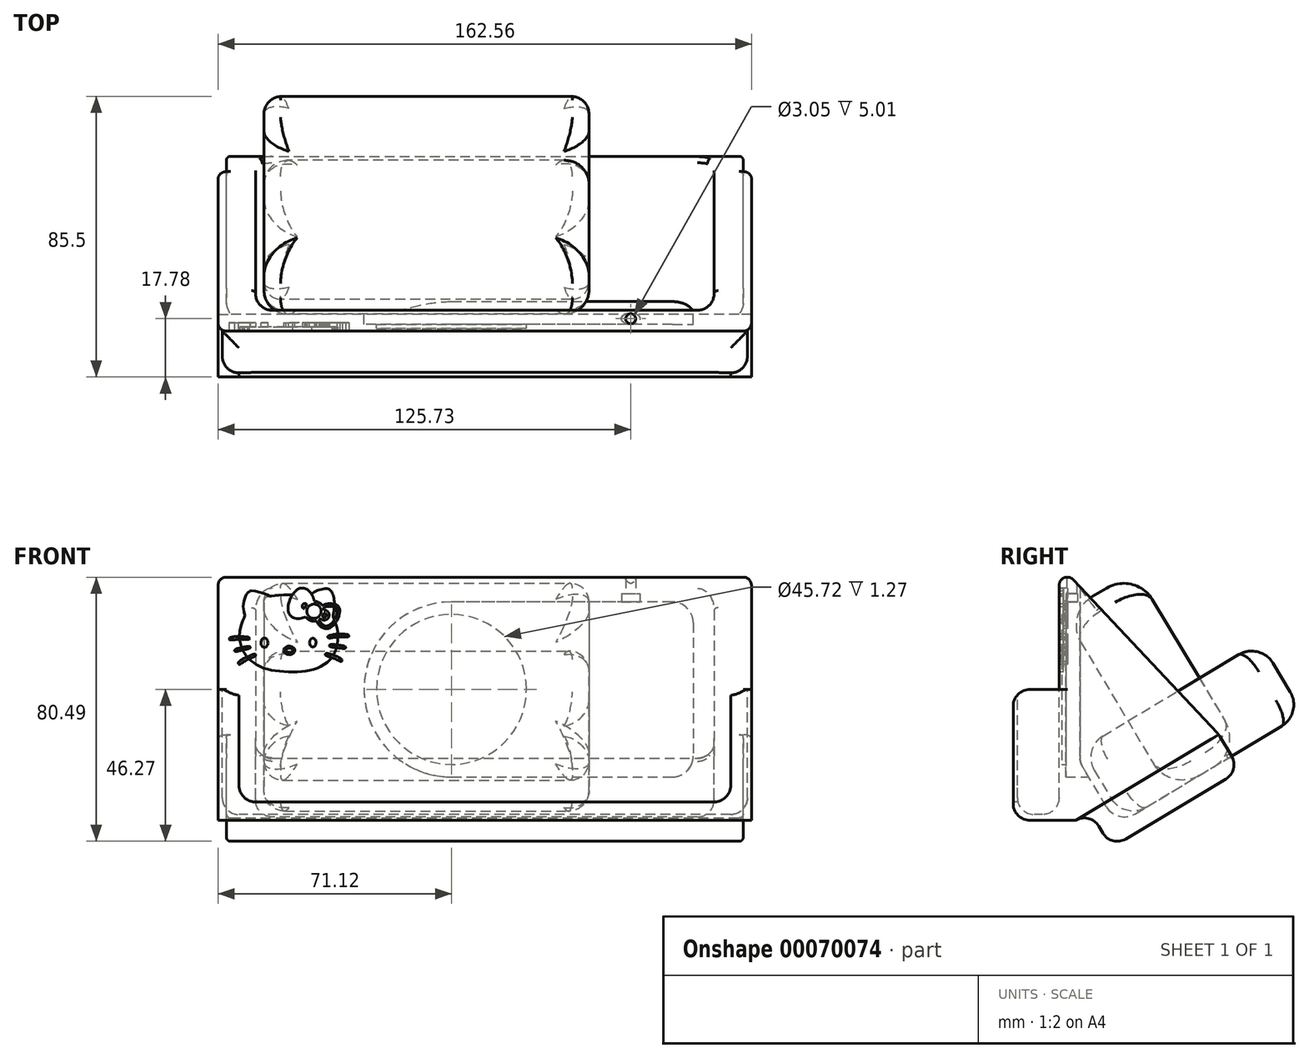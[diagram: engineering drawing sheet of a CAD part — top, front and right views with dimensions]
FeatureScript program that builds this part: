
annotation { "Feature Type Name" : "Feature", "Feature Type Description" : "" }
export const myFeature = defineFeature(function(context is Context, id is Id, definition is map)
    precondition{}
    {
        {
            var Q0;
            Q0=qCreatedBy(makeId("Right.planeOp"),FACE);
            var sketch = newSketch(context, id + "F0", { "sketchPlane" : qUnion([Q0])});
            skLineSegment(sketch, "E0", {"start": v(0, 0) * mm, "end": v(0, -76.2) * mm});
            skLineSegment(sketch, "E1", {"start": v(-13.97, -77.98) * mm, "end": v(5.08, -77.98) * mm});
            skLineSegment(sketch, "E2", {"start": v(0, -76.2) * mm, "end": v(-12.7, -76.2) * mm});
            skLineSegment(sketch, "E3", {"start": v(-12.7, -76.2) * mm, "end": v(-12.7, -72.4) * mm});
            skLineSegment(sketch, "E4", {"start": v(-12.7, -72.4) * mm, "end": v(-13.97, -72.4) * mm});
            skLineSegment(sketch, "E5", {"start": v(-13.97, -72.4) * mm, "end": v(-13.97, -77.98) * mm});
            skPoint(sketch, "E6.visualSharp", {"position": v(-12.7, -76.2) * mm});
            skPoint(sketch, "E7.visualSharp", {"position": v(0, -76.2) * mm});
            skPoint(sketch, "E8.visualSharp", {"position": v(-13.97, -77.98) * mm});
            skLineSegment(sketch, "E9", {"start": v(48.66, -51.87) * mm, "end": v(5.08, -77.98) * mm, "construction": true});
            skLineSegment(sketch, "E10", {"start": v(48.66, -51.87) * mm, "end": v(0, 0) * mm});
            skLineSegment(sketch, "E11", {"start": v(9.44, -75.37) * mm, "end": v(15.96, -86.26) * mm});
            skLineSegment(sketch, "E12", {"start": v(15.96, -86.26) * mm, "end": v(55.18, -62.76) * mm});
            skLineSegment(sketch, "E13", {"start": v(48.66, -51.87) * mm, "end": v(55.18, -62.76) * mm});
            skLineSegment(sketch, "E14", {"start": v(5.08, -77.98) * mm, "end": v(9.44, -75.37) * mm});
            skSolve(sketch);
        }
        {
            var Q0;
            Q0=qSketchRegion(id+"F0",true);
            extrude(context, id + "F1", {"entities" : qUnion([Q0]), "depth" : 81.28 * mm});
        }
        {
            var Q0;
            Q0=makeQuery(id+"F1.opExtrude","CAP_FACE",FACE,{"disambiguationData":[OSD([sQuery(id+"F0.wireOp",EDGE,"E0"),sQuery(id+"F0.wireOp",EDGE,"E1"),sQuery(id+"F0.wireOp",EDGE,"E2"),sQuery(id+"F0.wireOp",EDGE,"E3"),sQuery(id+"F0.wireOp",EDGE,"E4"),sQuery(id+"F0.wireOp",EDGE,"E5"),sQuery(id+"F0.wireOp",EDGE,"E9"),sQuery(id+"F0.wireOp",EDGE,"E10")])],"isStart":false});
            var sketch = newSketch(context, id + "F2", { "sketchPlane" : qUnion([Q0])});
            skLineSegment(sketch, "E15.bottom", {"start": v(-13.97, -77.98) * mm, "end": v(0, -77.98) * mm});
            skLineSegment(sketch, "E15.top", {"start": v(-13.97, -38.1) * mm, "end": v(0, -38.1) * mm});
            skLineSegment(sketch, "E15.left", {"start": v(-13.97, -77.98) * mm, "end": v(-13.97, -38.1) * mm});
            skLineSegment(sketch, "E15.right", {"start": v(0, -77.98) * mm, "end": v(0, -38.1) * mm});
            skSolve(sketch);
        }
        {
            var Q0;
            Q0=qSketchRegion(id+"F2",true);
            extrude(context, id + "F3", {"entities" : qUnion([Q0]), "operationType" : NewBodyOperationType.ADD, "oppositeDirection" : true, "depth" : 1.27 * mm});
        }
        {
            var Q0;
            Q0=makeQuery(id+"F3.boolean.opBoolean","MERGE",FACE,{"derivedFrom":[makeQuery(id+"F1.opExtrude","SWEPT_FACE",FACE,{"disambiguationData":[OSD([sQuery(id+"F0.wireOp",EDGE,"E5")])]}),makeQuery(id+"F3.opExtrude","SWEPT_FACE",FACE,{"disambiguationData":[OSD([sQuery(id+"F2.wireOp",EDGE,"E15.left")])]})]});
            var sketch = newSketch(context, id + "F4", { "sketchPlane" : qUnion([Q0])});
            skLineSegment(sketch, "E16.bottom", {"start": v(81.28, -77.98) * mm, "end": v(74.93, -77.98) * mm});
            skLineSegment(sketch, "E16.top", {"start": v(81.28, -38.1) * mm, "end": v(74.93, -38.1) * mm});
            skLineSegment(sketch, "E16.left", {"start": v(81.28, -77.98) * mm, "end": v(81.28, -38.1) * mm});
            skLineSegment(sketch, "E16.right", {"start": v(74.93, -77.98) * mm, "end": v(74.93, -38.1) * mm});
            skSolve(sketch);
        }
        {
            var Q0;
            Q0=qSketchRegion(id+"F4",true);
            extrude(context, id + "F5", {"entities" : qUnion([Q0]), "operationType" : NewBodyOperationType.ADD, "oppositeDirection" : true, "depth" : 1.27 * mm});
        }
        {
            var Q0;
            Q0=makeQuery(id+"F3.boolean.opBoolean","MERGE",FACE,{"derivedFrom":[makeQuery(id+"F1.opExtrude","CAP_FACE",FACE,{"disambiguationData":[OSD([sQuery(id+"F0.wireOp",EDGE,"E0"),sQuery(id+"F0.wireOp",EDGE,"E1"),sQuery(id+"F0.wireOp",EDGE,"E2"),sQuery(id+"F0.wireOp",EDGE,"E3"),sQuery(id+"F0.wireOp",EDGE,"E4"),sQuery(id+"F0.wireOp",EDGE,"E5"),sQuery(id+"F0.wireOp",EDGE,"E10"),sQuery(id+"F0.wireOp",EDGE,"E11"),sQuery(id+"F0.wireOp",EDGE,"E12"),sQuery(id+"F0.wireOp",EDGE,"E13"),sQuery(id+"F0.wireOp",EDGE,"E14")])],"isStart":false}),makeQuery(id+"F3.opExtrude","CAP_FACE",FACE,{"disambiguationData":[OSD([sQuery(id+"F2.wireOp",EDGE,"E15.bottom"),sQuery(id+"F2.wireOp",EDGE,"E15.top"),sQuery(id+"F2.wireOp",EDGE,"E15.left"),sQuery(id+"F2.wireOp",EDGE,"E15.right")])],"isStart":true})]});
            var sketch = newSketch(context, id + "F6", { "sketchPlane" : qUnion([Q0])});
            skLineSegment(sketch, "E17", {"start": v(65.06, -42.04) * mm, "end": v(-9.06, -86.45) * mm});
            skLineSegment(sketch, "E18", {"start": v(-9.06, -86.45) * mm, "end": v(1.92, -104.78) * mm});
            skLineSegment(sketch, "E19", {"start": v(1.92, -104.78) * mm, "end": v(76.04, -60.37) * mm});
            skLineSegment(sketch, "E20", {"start": v(76.04, -60.37) * mm, "end": v(65.06, -42.04) * mm});
            skSolve(sketch);
        }
        {
            var Q0;
            Q0=makeQuery(id+"F1.opExtrude","SWEPT_EDGE",EDGE,{"disambiguationData":[OSD([sQuery(id+"F0.wireOp",EDGE,"E0"),sQuery(id+"F0.wireOp",EDGE,"E10")])]});
            fillet(context, id + "F7", {"entities" : qUnion([Q0]), "radius" : 2.54 * mm, "tangentPropagation" : true, "allowEdgeOverflow" : false});
        }
        {
            var Q0;
            Q0=makeQuery(id+"F3.opExtrude","SWEPT_EDGE",EDGE,{"disambiguationData":[OSD([sQuery(id+"F0.wireOp",EDGE,"E0"),sQuery(id+"F2.wireOp",EDGE,"E15.top"),sQuery(id+"F2.wireOp",EDGE,"E15.right")])]});
            var Q1;
            Q1=makeQuery(id+"F5.boolean.opBoolean","MERGE",EDGE,{"derivedFrom":[makeQuery(id+"F3.opExtrude","SWEPT_EDGE",EDGE,{"disambiguationData":[OSD([sQuery(id+"F2.wireOp",EDGE,"E15.top"),sQuery(id+"F2.wireOp",EDGE,"E15.left")])]}),makeQuery(id+"F5.opExtrude","CAP_EDGE",EDGE,{"disambiguationData":[OSD([sQuery(id+"F4.wireOp",EDGE,"E16.top")])],"isStart":true})]});
            var Q2;
            Q2=makeQuery(id+"F5.boolean.opBoolean","INTERSECT",EDGE,{"derivedFrom":[makeQuery(id+"F1.opExtrude","SWEPT_FACE",FACE,{"disambiguationData":[OSD([sQuery(id+"F0.wireOp",EDGE,"E4")])]}),makeQuery(id+"F5.opExtrude","SWEPT_FACE",FACE,{"disambiguationData":[OSD([sQuery(id+"F4.wireOp",EDGE,"E16.right")])]})]});
            fillet(context, id + "F8", {"entities" : qUnion([Q0, Q1, Q2]), "radius" : 5.08 * mm, "tangentPropagation" : true, "allowEdgeOverflow" : false});
        }
        {
            var Q0;
            Q0=makeQuery(id+"F1.opExtrude","SWEPT_EDGE",EDGE,{"disambiguationData":[OSD([sQuery(id+"F0.wireOp",EDGE,"E0"),sQuery(id+"F0.wireOp",EDGE,"E2")])]});
            var Q1;
            Q1=makeQuery(id+"F1.opExtrude","SWEPT_EDGE",EDGE,{"disambiguationData":[OSD([sQuery(id+"F0.wireOp",EDGE,"E2"),sQuery(id+"F0.wireOp",EDGE,"E3")])]});
            var Q2;
            Q2=makeQuery(id+"F3.opExtrude","CAP_EDGE",EDGE,{"disambiguationData":[OSD([sQuery(id+"F2.wireOp",EDGE,"E15.right")])],"isStart":false});
            var Q3;
            Q3=makeQuery(id+"F5.boolean.opBoolean","INTERSECT",EDGE,{"derivedFrom":[makeQuery(id+"F3.opExtrude","CAP_FACE",FACE,{"disambiguationData":[OSD([sQuery(id+"F2.wireOp",EDGE,"E15.bottom"),sQuery(id+"F2.wireOp",EDGE,"E15.top"),sQuery(id+"F2.wireOp",EDGE,"E15.left"),sQuery(id+"F2.wireOp",EDGE,"E15.right")])],"isStart":false}),makeQuery(id+"F5.opExtrude","CAP_FACE",FACE,{"disambiguationData":[OSD([sQuery(id+"F4.wireOp",EDGE,"E16.bottom"),sQuery(id+"F4.wireOp",EDGE,"E16.top"),sQuery(id+"F4.wireOp",EDGE,"E16.left"),sQuery(id+"F4.wireOp",EDGE,"E16.right")])],"isStart":false})]});
            var Q4;
            Q4=makeQuery(id+"F3.boolean.opBoolean","INTERSECT",EDGE,{"derivedFrom":[makeQuery(id+"F1.opExtrude","SWEPT_FACE",FACE,{"disambiguationData":[OSD([sQuery(id+"F0.wireOp",EDGE,"E2")])]}),makeQuery(id+"F3.opExtrude","CAP_FACE",FACE,{"disambiguationData":[OSD([sQuery(id+"F2.wireOp",EDGE,"E15.bottom"),sQuery(id+"F2.wireOp",EDGE,"E15.top"),sQuery(id+"F2.wireOp",EDGE,"E15.left"),sQuery(id+"F2.wireOp",EDGE,"E15.right")])],"isStart":false})]});
            fillet(context, id + "F9", {"entities" : qUnion([Q0, Q1, Q2, Q3, Q4]), "radius" : 5.08 * mm, "tangentPropagation" : true, "allowEdgeOverflow" : false});
        }
        {
            var Q0;
            Q0=makeQuery(id+"FW1ILFxsN4tAGCR_1.boolean.opBoolean","COPY",EDGE,{"derivedFrom":makeQuery(id+"FW1ILFxsN4tAGCR_1.opExtrude","SWEPT_EDGE",EDGE,{"disambiguationData":[OSD([sQuery(id+"F2NUu0aQqmdHJ40_1.wireOp",EDGE,"11d1aa15-99fe-4fb5-b1c5-774e2ddcd56e.bottom"),sQuery(id+"F2NUu0aQqmdHJ40_1.wireOp",EDGE,"11d1aa15-99fe-4fb5-b1c5-774e2ddcd56e.left")])]})});
            var Q1;
            Q1=makeQuery(id+"F1.opExtrude","SWEPT_EDGE",EDGE,{"disambiguationData":[OSD([sQuery(id+"F0.wireOp",EDGE,"E1"),sQuery(id+"F0.wireOp",EDGE,"E5")])]});
            var Q2;
            Q2=makeQuery(id+"F1.opExtrude","SWEPT_EDGE",EDGE,{"disambiguationData":[OSD([sQuery(id+"F0.wireOp",EDGE,"E10"),sQuery(id+"F0.wireOp",EDGE,"E13")])]});
            var Q3;
            Q3=makeQuery(id+"F1.opExtrude","SWEPT_EDGE",EDGE,{"disambiguationData":[OSD([sQuery(id+"F0.wireOp",EDGE,"E12"),sQuery(id+"F0.wireOp",EDGE,"E13")])]});
            var Q4;
            Q4=makeQuery(id+"F1.opExtrude","SWEPT_EDGE",EDGE,{"disambiguationData":[OSD([sQuery(id+"F0.wireOp",EDGE,"E11"),sQuery(id+"F0.wireOp",EDGE,"E12")])]});
            var Q5;
            Q5=makeQuery(id+"F1.opExtrude","SWEPT_EDGE",EDGE,{"disambiguationData":[OSD([sQuery(id+"F0.wireOp",EDGE,"E11"),sQuery(id+"F0.wireOp",EDGE,"E14")])]});
            fillet(context, id + "F10", {"entities" : qUnion([Q0, Q1, Q2, Q3, Q4, Q5]), "radius" : 5.08 * mm, "tangentPropagation" : true, "allowEdgeOverflow" : false});
        }
        {
            var Q0;
            Q0=qSketchRegion(id+"F6",true);
            extrude(context, id + "F11", {"entities" : qUnion([Q0]), "operationType" : NewBodyOperationType.REMOVE, "oppositeDirection" : true, "depth" : 2.54 * mm});
        }
        {
            var Q0;
            Q0=makeQuery(id+"FW1ILFxsN4tAGCR_1.boolean.opBoolean","INTERSECT",EDGE,{"derivedFrom":[makeQuery(id+"F1.opExtrude","SWEPT_FACE",FACE,{"disambiguationData":[OSD([sQuery(id+"F0.wireOp",EDGE,"E10")])]}),makeQuery(id+"FW1ILFxsN4tAGCR_1.opExtrude","SWEPT_FACE",FACE,{"disambiguationData":[OSD([sQuery(id+"F2NUu0aQqmdHJ40_1.wireOp",EDGE,"11d1aa15-99fe-4fb5-b1c5-774e2ddcd56e.left")])]})]});
            var Q1;
            Q1=makeQuery(id+"F1.opExtrude","CAP_EDGE",EDGE,{"disambiguationData":[OSD([sQuery(id+"F0.wireOp",EDGE,"E10")])],"isStart":false});
            var Q2;
            Q2=makeQuery(id+"F11.boolean.opBoolean","COPY",EDGE,{"derivedFrom":makeQuery(id+"F11.opExtrude","CAP_EDGE",EDGE,{"disambiguationData":[OSD([sQuery(id+"F6.wireOp",EDGE,"E17")])],"isStart":true})});
            fillet(context, id + "F12", {"entities" : qUnion([Q0, Q1, Q2]), "radius" : 2.54 * mm, "tangentPropagation" : true, "allowEdgeOverflow" : false});
        }
        {
            var Q0;
            Q0=makeQuery(id+"F11.boolean.opBoolean","INTERSECT",EDGE,{"derivedFrom":[makeQuery(id+"F1.opExtrude","SWEPT_FACE",FACE,{"disambiguationData":[OSD([sQuery(id+"F0.wireOp",EDGE,"E12")])]}),makeQuery(id+"F11.opExtrude","CAP_FACE",FACE,{"disambiguationData":[OSD([sQuery(id+"F6.wireOp",EDGE,"E17"),sQuery(id+"F6.wireOp",EDGE,"E18"),sQuery(id+"F6.wireOp",EDGE,"E19"),sQuery(id+"F6.wireOp",EDGE,"E20")])],"isStart":false})]});
            fillet(context, id + "F13", {"entities" : qUnion([Q0]), "radius" : 1.27 * mm, "tangentPropagation" : true, "allowEdgeOverflow" : false});
        }
        {
            var Q0;
            Q0=makeQuery(id+"F1.opExtrude","CAP_FACE",FACE,{"disambiguationData":[OSD([sQuery(id+"F0.wireOp",EDGE,"E0"),sQuery(id+"F0.wireOp",EDGE,"E1"),sQuery(id+"F0.wireOp",EDGE,"E2"),sQuery(id+"F0.wireOp",EDGE,"E3"),sQuery(id+"F0.wireOp",EDGE,"E4"),sQuery(id+"F0.wireOp",EDGE,"E5"),sQuery(id+"F0.wireOp",EDGE,"E10"),sQuery(id+"F0.wireOp",EDGE,"E11"),sQuery(id+"F0.wireOp",EDGE,"E12"),sQuery(id+"F0.wireOp",EDGE,"E13"),sQuery(id+"F0.wireOp",EDGE,"E14")])],"isStart":true});
            var sketch = newSketch(context, id + "F14", { "sketchPlane" : qUnion([Q0])});
            skLineSegment(sketch, "E21.bottom", {"start": v(-6.35, 2.74) * mm, "end": v(-69.85, 2.74) * mm});
            skLineSegment(sketch, "E21.left", {"start": v(-6.35, 2.74) * mm, "end": v(-6.35, -58.57) * mm});
            skLineSegment(sketch, "E21.right", {"start": v(-69.85, 2.74) * mm, "end": v(-69.85, -48.06) * mm});
            skLineSegment(sketch, "E22", {"start": v(-23.16, -76.03) * mm, "end": v(-69.85, -48.06) * mm});
            skLineSegment(sketch, "E23", {"start": v(-14.45, -73.85) * mm, "end": v(-7.25, -61.84) * mm});
            skPoint(sketch, "E24.visualSharp", {"position": v(-17.71, -79.3) * mm});
            skArc(sketch, "E24.filletArc", {"start": v(-23.16, -76.03) * mm, "mid": v(-18.35, -76.74) * mm, "end": v(-14.45, -73.85) * mm});
            skPoint(sketch, "E21.top.end.orphan", {"position": v(-69.85, -98.86) * mm});
            skPoint(sketch, "E25.visualSharp", {"position": v(-6.35, -60.33) * mm});
            skArc(sketch, "E25.filletArc", {"start": v(-7.25, -61.84) * mm, "mid": v(-6.58, -60.27) * mm, "end": v(-6.35, -58.57) * mm});
            skSolve(sketch);
        }
        {
            var Q0;
            Q0 = qSketchRegion(id + "F14", true);
            extrude(context, id + "F15", {"entities" : qUnion([Q0]), "operationType" : NewBodyOperationType.REMOVE, "oppositeDirection" : true, "depth" : 69.85 * mm});
        }
        {
            var Q0;
            Q0=makeQuery(id+"F15.boolean.opBoolean","COPY",EDGE,{"derivedFrom":makeQuery(id+"F15.opExtrude","CAP_EDGE",EDGE,{"disambiguationData":[OSD([sQuery(id+"F14.wireOp",EDGE,"E22")])],"isStart":false})});
            fillet(context, id + "F16", {"entities" : qUnion([Q0]), "radius" : 5.08 * mm, "tangentPropagation" : true, "allowEdgeOverflow" : false});
        }
        {
            var Q0;
            Q0=makeQuery(id+"F15.boolean.opBoolean","INTERSECT",EDGE,{"derivedFrom":[makeQuery(id+"F1.opExtrude","SWEPT_FACE",FACE,{"disambiguationData":[OSD([sQuery(id+"F0.wireOp",EDGE,"E10")])]}),makeQuery(id+"F15.opExtrude","CAP_FACE",FACE,{"disambiguationData":[OSD([sQuery(id+"F14.wireOp",EDGE,"E21.bottom"),sQuery(id+"F14.wireOp",EDGE,"E21.left"),sQuery(id+"F14.wireOp",EDGE,"E21.right"),sQuery(id+"F14.wireOp",EDGE,"E22"),sQuery(id+"F14.wireOp",EDGE,"E23"),sQuery(id+"F14.wireOp",EDGE,"E24.filletArc"),sQuery(id+"F14.wireOp",EDGE,"E25.filletArc")])],"isStart":false})]});
            fillet(context, id + "F17", {"entities" : qUnion([Q0]), "radius" : 1.27 * mm, "tangentPropagation" : true, "allowEdgeOverflow" : false});
        }
        {
            var Q0;
            Q0=makeQuery(id+"F1.opExtrude","SWEPT_BODY",BODY,{"disambiguationData":[OSD([sQuery(id+"F0.wireOp",EDGE,"E0"),sQuery(id+"F0.wireOp",EDGE,"E1"),sQuery(id+"F0.wireOp",EDGE,"E2"),sQuery(id+"F0.wireOp",EDGE,"E3"),sQuery(id+"F0.wireOp",EDGE,"E4"),sQuery(id+"F0.wireOp",EDGE,"E5"),sQuery(id+"F0.wireOp",EDGE,"E9"),sQuery(id+"F0.wireOp",EDGE,"E10")])]});
            var Q1;
            Q1=makeQuery(id+"F1.opExtrude","CAP_FACE",FACE,{"disambiguationData":[OSD([sQuery(id+"F0.wireOp",EDGE,"E0"),sQuery(id+"F0.wireOp",EDGE,"E1"),sQuery(id+"F0.wireOp",EDGE,"E2"),sQuery(id+"F0.wireOp",EDGE,"E3"),sQuery(id+"F0.wireOp",EDGE,"E4"),sQuery(id+"F0.wireOp",EDGE,"E5"),sQuery(id+"F0.wireOp",EDGE,"E9"),sQuery(id+"F0.wireOp",EDGE,"E10")])],"isStart":true});
            mirror(context, id + "F18", {"operationType" : NewBodyOperationType.ADD, "entities" : qUnion([Q0]), "mirrorPlane" : qUnion([Q1])});
        }
        {
            var Q0;
            {var subQ0=makeQuery(id+"F1.opExtrude","SWEPT_FACE",FACE,{"disambiguationData":[OSD([sQuery(id+"F0.wireOp",EDGE,"E0")])]});Q0=makeQuery(id+"F18.boolean.opBoolean","MERGE",FACE,{"derivedFrom":[subQ0,makeQuery(id+"F18.opPattern","COPY",FACE,{"derivedFrom":subQ0,"instanceName":"1"})]});}
            var sketch = newSketch(context, id + "F19", { "sketchPlane" : qUnion([Q0])});
            skFitSpline(sketch, "E26", {"points": [v(-73.1, -15.58) * mm, v(-73.63, -13.12) * mm, v(-73.13, -10.13) * mm, v(-72.68, -9.23) * mm, v(-71.74, -8.23) * mm, v(-70.06, -8.08) * mm, v(-67.22, -8.9) * mm, v(-66.07, -9.41) * mm, v(-65.52, -9.65) * mm, v(-64.9, -9.7) * mm, v(-63.16, -9.43) * mm, v(-60.43, -9.3) * mm, v(-57.93, -9.32) * mm, v(-54.78, -9.57) * mm, v(-54.26, -9.63) * mm, v(-53.64, -9.46) * mm, v(-52.25, -8.6) * mm, v(-50.23, -7.69) * mm, v(-48.43, -7.37) * mm, v(-47.52, -7.54) * mm, v(-47.03, -7.91) * mm, v(-46.38, -9) * mm, v(-45.95, -10.69) * mm, v(-45.8, -12.09) * mm, v(-45.86, -12.9) * mm, v(-46.14, -15.06) * mm, v(-46.28, -15.8) * mm, v(-46.18, -16.16) * mm, v(-45.22, -18.72) * mm, v(-44.77, -21.3) * mm, v(-44.96, -24.23) * mm, v(-45.67, -26.7) * mm, v(-47.2, -29.08) * mm, v(-50.84, -31.5) * mm, v(-55.83, -32.64) * mm, v(-61.98, -32.61) * mm, v(-67.36, -31.58) * mm, v(-70.82, -29.62) * mm, v(-72.91, -27.53) * mm, v(-74.17, -24.96) * mm, v(-74.78, -21.77) * mm, v(-74.06, -17.98) * mm, v(-73.2, -16) * mm, v(-73.1, -15.58) * mm]});
            skFitSpline(sketch, "E27.0", {"points": [v(-72.04, -15.67) * mm, v(-72.05, -15.45) * mm, v(-72.08, -15.27) * mm, v(-72.14, -15.04) * mm, v(-72.21, -14.77) * mm, v(-72.31, -14.42) * mm, v(-72.41, -14.05) * mm, v(-72.5, -13.66) * mm, v(-72.57, -13.28) * mm, v(-72.6, -12.92) * mm, v(-72.6, -12.54) * mm, v(-72.56, -12.15) * mm, v(-72.48, -11.64) * mm, v(-72.36, -11.15) * mm, v(-72.23, -10.73) * mm, v(-72.13, -10.46) * mm, v(-72.05, -10.26) * mm, v(-71.99, -10.11) * mm, v(-71.91, -9.98) * mm, v(-71.84, -9.86) * mm, v(-71.76, -9.74) * mm, v(-71.68, -9.62) * mm, v(-71.57, -9.47) * mm, v(-71.43, -9.32) * mm, v(-71.33, -9.22) * mm, v(-71.26, -9.17) * mm, v(-71.21, -9.14) * mm, v(-71.18, -9.12) * mm, v(-71.12, -9.1) * mm, v(-71.03, -9.08) * mm, v(-70.82, -9.05) * mm, v(-70.4, -9.07) * mm, v(-69.7, -9.21) * mm, v(-68.91, -9.42) * mm, v(-68.27, -9.63) * mm, v(-67.8, -9.8) * mm, v(-67.4, -9.96) * mm, v(-66.98, -10.14) * mm, v(-66.66, -10.3) * mm, v(-66.42, -10.41) * mm, v(-66.22, -10.51) * mm, v(-65.98, -10.61) * mm, v(-65.7, -10.7) * mm, v(-65.38, -10.75) * mm, v(-65.07, -10.76) * mm, v(-64.77, -10.74) * mm, v(-64.37, -10.68) * mm, v(-63.86, -10.6) * mm, v(-63.3, -10.5) * mm, v(-62.84, -10.45) * mm, v(-62.36, -10.4) * mm, v(-61.45, -10.36) * mm, v(-60.4, -10.35) * mm, v(-59.47, -10.34) * mm, v(-58.77, -10.34) * mm, v(-57.99, -10.37) * mm, v(-57.2, -10.4) * mm, v(-56.57, -10.45) * mm, v(-56.11, -10.49) * mm, v(-55.68, -10.53) * mm, v(-55.3, -10.56) * mm, v(-55.05, -10.6) * mm, v(-54.9, -10.61) * mm, v(-54.78, -10.63) * mm, v(-54.66, -10.65) * mm, v(-54.5, -10.67) * mm, v(-54.36, -10.68) * mm, v(-54.2, -10.68) * mm, v(-54, -10.66) * mm, v(-53.74, -10.61) * mm, v(-53.48, -10.53) * mm, v(-53.28, -10.45) * mm, v(-53.07, -10.35) * mm, v(-52.83, -10.21) * mm, v(-52.55, -10.04) * mm, v(-52.28, -9.87) * mm, v(-52.02, -9.7) * mm, v(-51.75, -9.53) * mm, v(-51.4, -9.32) * mm, v(-50.91, -9.07) * mm, v(-50.32, -8.82) * mm, v(-49.72, -8.62) * mm, v(-49.14, -8.48) * mm, v(-48.7, -8.43) * mm, v(-48.43, -8.41) * mm, v(-48.26, -8.42) * mm, v(-48.12, -8.44) * mm, v(-48.01, -8.47) * mm, v(-47.94, -8.5) * mm, v(-47.91, -8.51) * mm, v(-47.9, -8.52) * mm, v(-47.85, -8.56) * mm, v(-47.76, -8.67) * mm, v(-47.66, -8.8) * mm, v(-47.55, -8.98) * mm, v(-47.45, -9.17) * mm, v(-47.36, -9.38) * mm, v(-47.24, -9.68) * mm, v(-47.12, -10.1) * mm, v(-47.03, -10.58) * mm, v(-46.96, -10.98) * mm, v(-46.92, -11.28) * mm, v(-46.88, -11.55) * mm, v(-46.86, -11.8) * mm, v(-46.85, -12.02) * mm, v(-46.84, -12.17) * mm, v(-46.85, -12.3) * mm, v(-46.87, -12.45) * mm, v(-46.9, -12.67) * mm, v(-46.94, -13.08) * mm, v(-47, -13.56) * mm, v(-47.05, -14.07) * mm, v(-47.1, -14.43) * mm, v(-47.14, -14.75) * mm, v(-47.2, -14.99) * mm, v(-47.24, -15.2) * mm, v(-47.28, -15.38) * mm, v(-47.32, -15.56) * mm, v(-47.33, -15.72) * mm, v(-47.34, -15.93) * mm, v(-47.3, -16.14) * mm, v(-47.25, -16.3) * mm, v(-47.2, -16.43) * mm, v(-47.17, -16.53) * mm, v(-47.11, -16.66) * mm, v(-47.02, -16.88) * mm, v(-46.89, -17.2) * mm, v(-46.74, -17.57) * mm, v(-46.59, -17.97) * mm, v(-46.43, -18.39) * mm, v(-46.3, -18.8) * mm, v(-46.17, -19.18) * mm, v(-46.04, -19.66) * mm, v(-45.92, -20.21) * mm, v(-45.85, -20.75) * mm, v(-45.82, -21.2) * mm, v(-45.8, -21.67) * mm, v(-45.82, -22.56) * mm, v(-45.91, -23.62) * mm, v(-46.09, -24.58) * mm, v(-46.26, -25.25) * mm, v(-46.47, -25.89) * mm, v(-46.73, -26.52) * mm, v(-47.04, -27.13) * mm, v(-47.4, -27.71) * mm, v(-47.79, -28.18) * mm, v(-48.15, -28.55) * mm, v(-48.56, -28.92) * mm, v(-49.14, -29.38) * mm, v(-49.93, -29.88) * mm, v(-50.78, -30.34) * mm, v(-51.67, -30.72) * mm, v(-52.6, -31.02) * mm, v(-53.89, -31.35) * mm, v(-55.61, -31.6) * mm, v(-57.86, -31.73) * mm, v(-59.81, -31.7) * mm, v(-61.37, -31.61) * mm, v(-62.91, -31.48) * mm, v(-64.39, -31.29) * mm, v(-65.75, -31) * mm, v(-66.7, -30.72) * mm, v(-67.56, -30.38) * mm, v(-68.65, -29.85) * mm, v(-69.62, -29.22) * mm, v(-70.5, -28.55) * mm, v(-71.08, -28.05) * mm, v(-71.59, -27.53) * mm, v(-72.02, -27) * mm, v(-72.39, -26.43) * mm, v(-72.72, -25.79) * mm, v(-73, -25.1) * mm, v(-73.27, -24.36) * mm, v(-73.49, -23.62) * mm, v(-73.65, -22.87) * mm, v(-73.72, -22.24) * mm, v(-73.73, -21.72) * mm, v(-73.72, -21.18) * mm, v(-73.64, -20.47) * mm, v(-73.46, -19.6) * mm, v(-73.27, -18.9) * mm, v(-73.09, -18.36) * mm, v(-72.94, -17.98) * mm, v(-72.8, -17.61) * mm, v(-72.65, -17.28) * mm, v(-72.5, -16.98) * mm, v(-72.38, -16.72) * mm, v(-72.3, -16.54) * mm, v(-72.24, -16.43) * mm, v(-72.18, -16.31) * mm, v(-72.11, -16.14) * mm, v(-72.06, -15.91) * mm, v(-72.04, -15.67) * mm, v(-72.05, -15.45) * mm, v(-72.08, -15.27) * mm]});
            skFitSpline(sketch, "E28", {"points": [v(-72.34, -14.3) * mm, v(-72.22, -14.48) * mm, v(-72, -14.43) * mm, v(-71.72, -14.3) * mm, v(-71.38, -14.4) * mm, v(-71.27, -14.7) * mm, v(-71.32, -15) * mm, v(-71.61, -15.41) * mm, v(-71.9, -15.87) * mm, v(-72.12, -16.15) * mm], "startDerivative": vector(0.87, -3.5) * mm, "endDerivative": vector(-1.74, -4.2) * mm});
            skSolve(sketch);
        }
        {
            var Q0;
            Q0=qSketchRegion(id+"F19",true);
            extrude(context, id + "F20", {"entities" : qUnion([Q0]), "operationType" : NewBodyOperationType.REMOVE, "oppositeDirection" : true, "depth" : 1.27 * mm});
        }
        {
            var Q0;
            Q0=makeQuery(id+"F19.imprint","IMPRINT",FACE,{"disambiguationData":[TD([[makeQuery(id+"F19.imprint","IMPRINT",EDGE,{"derivedFrom":sQuery(id+"F19.wireOp",EDGE,"E26")}),1.0]])]});
            var sketch = newSketch(context, id + "F21", { "sketchPlane" : qUnion([Q0])});
            skFitSpline(sketch, "E29", {"points": [v(-75.23, -21.92) * mm, v(-72.85, -22.06) * mm, v(-71.94, -22.25) * mm, v(-71.67, -22.52) * mm, v(-71.73, -22.73) * mm, v(-72.07, -22.88) * mm, v(-73.22, -22.82) * mm, v(-75.38, -22.84) * mm, v(-77.02, -23.01) * mm, v(-77.62, -23.01) * mm, v(-77.88, -22.9) * mm, v(-77.87, -22.54) * mm, v(-76.9, -22.1) * mm, v(-75.23, -21.92) * mm]});
            skFitSpline(sketch, "E30", {"points": [v(-74.52, -25.4) * mm, v(-72.45, -25.02) * mm, v(-71.65, -25.06) * mm, v(-71.48, -25.2) * mm, v(-71.53, -25.46) * mm, v(-71.67, -25.56) * mm, v(-72.3, -25.75) * mm, v(-74.29, -26.2) * mm, v(-75.67, -26.55) * mm, v(-76.03, -26.55) * mm, v(-76.28, -26.34) * mm, v(-76.2, -26.1) * mm, v(-75.36, -25.63) * mm, v(-74.52, -25.4) * mm]});
            skFitSpline(sketch, "E31", {"points": [v(-73.28, -28.58) * mm, v(-71.17, -27.62) * mm, v(-70.28, -27.32) * mm, v(-69.93, -27.36) * mm, v(-69.84, -27.53) * mm, v(-69.83, -27.72) * mm, v(-70.07, -27.98) * mm, v(-72.42, -29.06) * mm, v(-73.97, -30) * mm, v(-74.58, -30.41) * mm, v(-74.91, -30.4) * mm, v(-75.13, -30.25) * mm, v(-75.1, -29.9) * mm, v(-74.43, -29.25) * mm, v(-73.28, -28.58) * mm]});
            skEllipse(sketch, "E32", {"center": v(-67.16, -23.85) * mm, "majorRadius": 1.43 * mm, "minorRadius": 1.09 * mm, "majorAxis": v(0, 1)});
            skEllipse(sketch, "E33", {"center": v(-52.41, -23.8) * mm, "majorRadius": 1.34 * mm, "minorRadius": 0.98 * mm, "majorAxis": v(0, 1)});
            skEllipse(sketch, "E34", {"center": v(-59.58, -26.2) * mm, "majorRadius": 1.3 * mm, "minorRadius": 1.7 * mm, "majorAxis": v(0, 1)});
            skEllipse(sketch, "E35", {"center": v(-59.58, -26.2) * mm, "majorRadius": 0.7 * mm, "minorRadius": 1.07 * mm, "majorAxis": v(0, 1)});
            skFitSpline(sketch, "E36", {"points": [v(-47.35, -27.24) * mm, v(-45.12, -28.03) * mm, v(-43.72, -28.82) * mm, v(-43.46, -29.12) * mm, v(-43.55, -29.42) * mm, v(-43.7, -29.57) * mm, v(-44.34, -29.38) * mm, v(-46.32, -28.5) * mm, v(-48.12, -27.92) * mm, v(-48.5, -27.68) * mm, v(-48.57, -27.34) * mm, v(-48.3, -27.12) * mm, v(-47.35, -27.24) * mm]});
            skFitSpline(sketch, "E37", {"points": [v(-45.56, -24.45) * mm, v(-43.35, -24.77) * mm, v(-42.42, -25.13) * mm, v(-42.36, -25.3) * mm, v(-42.4, -25.48) * mm, v(-42.91, -25.6) * mm, v(-44.42, -25.46) * mm, v(-46.59, -25.19) * mm, v(-47.19, -24.98) * mm, v(-47.36, -24.75) * mm, v(-47.23, -24.48) * mm, v(-46.38, -24.4) * mm, v(-45.56, -24.45) * mm]});
            skFitSpline(sketch, "E38", {"points": [v(-44.68, -21.2) * mm, v(-43.6, -21.2) * mm, v(-42.23, -21.32) * mm, v(-41.52, -21.56) * mm, v(-41.4, -21.86) * mm, v(-41.64, -22.05) * mm, v(-42.64, -22.07) * mm, v(-45.04, -22.13) * mm, v(-46.24, -22.3) * mm, v(-47.4, -22.43) * mm, v(-47.77, -22.32) * mm, v(-47.87, -22.1) * mm, v(-47.8, -21.85) * mm, v(-47.34, -21.64) * mm, v(-45.56, -21.3) * mm, v(-44.68, -21.2) * mm]});
            skArc(sketch, "E39", {"start": v(-54.26, -12.19) * mm, "mid": v(-54.7, -12.8) * mm, "end": v(-54.98, -13.5) * mm});
            skCircle(sketch, "E40", {"center": v(-52.03, -14.27) * mm, "radius": 2.18 * mm});
            skArc(sketch, "E41", {"start": v(-54.26, -12.19) * mm, "mid": v(-55.57, -12.32) * mm, "end": v(-54.98, -13.5) * mm});
            skArc(sketch, "E42", {"start": v(-53.53, -11.62) * mm, "mid": v(-56.38, -11.87) * mm, "end": v(-55.07, -14.42) * mm});
            skArc(sketch, "E43", {"start": v(-49.45, -15.86) * mm, "mid": v(-48.34, -15.68) * mm, "end": v(-49.04, -14.8) * mm});
            skArc(sketch, "E44", {"start": v(-50.02, -16.54) * mm, "mid": v(-47.52, -16) * mm, "end": v(-49.01, -13.92) * mm});
            skArc(sketch, "E45.trimOffspring", {"start": v(-55.07, -14.42) * mm, "mid": v(-55.02, -14.84) * mm, "end": v(-54.91, -15.26) * mm});
            skArc(sketch, "E46.trimOffspring", {"start": v(-49.45, -15.86) * mm, "mid": v(-49.2, -15.35) * mm, "end": v(-49.04, -14.8) * mm});
            skArc(sketch, "E47.trimOffspring", {"start": v(-49.01, -13.92) * mm, "mid": v(-49.08, -13.56) * mm, "end": v(-49.18, -13.2) * mm});
            skFitSpline(sketch, "E48", {"points": [v(-51.9, -11.23) * mm, v(-52.92, -8.88) * mm, v(-55.02, -7.27) * mm, v(-56.9, -7.52) * mm, v(-58.2, -8.65) * mm, v(-59.1, -10) * mm, v(-59.89, -12.48) * mm, v(-59.87, -14.38) * mm, v(-59.1, -15.72) * mm, v(-57.8, -16.4) * mm, v(-56.06, -16.4) * mm, v(-54.56, -15.96) * mm], "startDerivative": vector(-8.54, 24.58) * mm, "endDerivative": vector(15.98, 7.04) * mm});
            skFitSpline(sketch, "E49.0", {"points": [v(-52.63, -11.49) * mm, v(-52.72, -11.22) * mm, v(-52.89, -10.73) * mm, v(-53.13, -10.08) * mm, v(-53.37, -9.6) * mm, v(-53.6, -9.26) * mm, v(-53.81, -9) * mm, v(-54.05, -8.75) * mm, v(-54.3, -8.52) * mm, v(-54.57, -8.33) * mm, v(-54.83, -8.17) * mm, v(-55.09, -8.05) * mm, v(-55.32, -7.99) * mm, v(-55.55, -7.96) * mm, v(-55.85, -7.97) * mm, v(-56.16, -8.04) * mm, v(-56.45, -8.16) * mm, v(-56.73, -8.32) * mm, v(-57.07, -8.58) * mm, v(-57.38, -8.9) * mm, v(-57.62, -9.18) * mm, v(-57.85, -9.45) * mm, v(-58.1, -9.79) * mm, v(-58.31, -10.17) * mm, v(-58.5, -10.55) * mm, v(-58.66, -10.97) * mm, v(-58.87, -11.55) * mm, v(-59.06, -12.27) * mm, v(-59.18, -12.93) * mm, v(-59.22, -13.5) * mm, v(-59.17, -14) * mm, v(-59.05, -14.44) * mm, v(-58.85, -14.84) * mm, v(-58.63, -15.1) * mm, v(-58.44, -15.28) * mm, v(-58.22, -15.42) * mm, v(-57.9, -15.57) * mm, v(-57.45, -15.68) * mm, v(-56.93, -15.71) * mm, v(-56.39, -15.68) * mm, v(-55.67, -15.55) * mm, v(-55.17, -15.37) * mm, v(-54.88, -15.24) * mm]});
            skArc(sketch, "E50.trimOffspring", {"start": v(-52.7, -11.3) * mm, "mid": v(-53.12, -11.43) * mm, "end": v(-53.53, -11.62) * mm});
            skArc(sketch, "E51.trimOffspring", {"start": v(-54.56, -15.96) * mm, "mid": v(-53.11, -17.11) * mm, "end": v(-51.26, -17.2) * mm});
            skFitSpline(sketch, "E52", {"points": [v(-49.57, -12.49) * mm, v(-47.96, -12.01) * mm, v(-45.65, -12.15) * mm, v(-44.72, -12.66) * mm, v(-44.28, -13.56) * mm, v(-44.43, -15.54) * mm, v(-45.25, -17.44) * mm, v(-46.65, -18.94) * mm, v(-48.12, -19.57) * mm, v(-49.63, -19.2) * mm, v(-50.77, -18.12) * mm, v(-51.26, -17.2) * mm], "startDerivative": vector(15.79, 6.36) * mm, "endDerivative": vector(-5.6, 12.22) * mm});
            skFitSpline(sketch, "E53.0", {"points": [v(-49.27, -13.24) * mm, v(-49.1, -13.17) * mm, v(-48.8, -13.05) * mm, v(-48.42, -12.93) * mm, v(-48.1, -12.85) * mm, v(-47.85, -12.81) * mm, v(-47.57, -12.78) * mm, v(-47.16, -12.77) * mm, v(-46.63, -12.79) * mm, v(-46.15, -12.86) * mm, v(-45.85, -12.93) * mm, v(-45.67, -12.99) * mm, v(-45.54, -13.05) * mm, v(-45.44, -13.1) * mm, v(-45.36, -13.17) * mm, v(-45.28, -13.25) * mm, v(-45.22, -13.33) * mm, v(-45.15, -13.44) * mm, v(-45.1, -13.6) * mm, v(-45.06, -13.82) * mm, v(-45.04, -14.1) * mm, v(-45.06, -14.55) * mm, v(-45.16, -15.12) * mm, v(-45.3, -15.68) * mm, v(-45.49, -16.2) * mm, v(-45.72, -16.67) * mm, v(-46.01, -17.13) * mm, v(-46.35, -17.57) * mm, v(-46.73, -17.97) * mm, v(-47.13, -18.3) * mm, v(-47.53, -18.56) * mm, v(-47.83, -18.69) * mm, v(-48.06, -18.74) * mm, v(-48.28, -18.77) * mm, v(-48.57, -18.76) * mm, v(-48.88, -18.67) * mm, v(-49.12, -18.56) * mm, v(-49.36, -18.43) * mm, v(-49.65, -18.2) * mm, v(-49.9, -17.93) * mm, v(-50.07, -17.7) * mm, v(-50.21, -17.5) * mm, v(-50.35, -17.24) * mm, v(-50.46, -17) * mm, v(-50.52, -16.87) * mm]});
            skArc(sketch, "E54.trimOffspring", {"start": v(-49.57, -12.49) * mm, "mid": v(-50.59, -11.6) * mm, "end": v(-51.9, -11.23) * mm});
            skArc(sketch, "E55.trimOffspring", {"start": v(-50.5, -16.9) * mm, "mid": v(-50.25, -16.73) * mm, "end": v(-50.02, -16.54) * mm});
            skSolve(sketch);
        }
        {
            var Q0;
            Q0=qSketchRegion(id+"F21",true);
            extrude(context, id + "F22", {"entities" : qUnion([Q0]), "operationType" : NewBodyOperationType.REMOVE, "oppositeDirection" : true, "depth" : 2.54 * mm});
        }
        {
            var Q0;
            {var subQ0=makeQuery(id+"F15.boolean.opBoolean","COPY",FACE,{"derivedFrom":makeQuery(id+"F15.opExtrude","SWEPT_FACE",FACE,{"disambiguationData":[OSD([sQuery(id+"F14.wireOp",EDGE,"E21.left")])]})});Q0=makeQuery(id+"F18.boolean.opBoolean","MERGE",FACE,{"derivedFrom":[subQ0,makeQuery(id+"F18.opPattern","COPY",FACE,{"derivedFrom":subQ0,"instanceName":"1"})]});}
            var sketch = newSketch(context, id + "F23", { "sketchPlane" : qUnion([Q0])});
            skCircle(sketch, "E56", {"center": v(10.16, -38.1) * mm, "radius": 22.86 * mm});
            skSolve(sketch);
        }
        {
            var Q0;
            Q0 = qSketchRegion(id + "F23", true);
            extrude(context, id + "F24", {"entities" : qUnion([Q0]), "operationType" : NewBodyOperationType.REMOVE, "oppositeDirection" : true, "depth" : 5.6 * mm, "hasSecondDirection" : true, "secondDirectionOppositeDirection" : false, "secondDirectionDepth" : 5.08 * mm});
        }
        {
            var Q0;
            {var subQ0=makeQuery(id+"F15.boolean.opBoolean","COPY",FACE,{"derivedFrom":makeQuery(id+"F15.opExtrude","SWEPT_FACE",FACE,{"disambiguationData":[OSD([sQuery(id+"F14.wireOp",EDGE,"E21.left")])]})});Q0=makeQuery(id+"F18.boolean.opBoolean","MERGE",FACE,{"derivedFrom":[subQ0,makeQuery(id+"F18.opPattern","COPY",FACE,{"derivedFrom":subQ0,"instanceName":"1"})]});}
            var sketch = newSketch(context, id + "F25", { "sketchPlane" : qUnion([Q0])});
            skArc(sketch, "E57", {"start": v(10.16, -64.77) * mm, "mid": v(36.83, -38.1) * mm, "end": v(10.16, -11.43) * mm});
            skLineSegment(sketch, "E58", {"start": v(-57.15, -11.43) * mm, "end": v(10.16, -11.43) * mm});
            skLineSegment(sketch, "E59", {"start": v(-63.5, -17.78) * mm, "end": v(-63.5, -58.42) * mm});
            skLineSegment(sketch, "E60", {"start": v(-57.15, -64.77) * mm, "end": v(10.16, -64.77) * mm});
            skPoint(sketch, "E61.visualSharp", {"position": v(-63.5, -11.43) * mm});
            skArc(sketch, "E61.filletArc", {"start": v(-57.15, -11.43) * mm, "mid": v(-61.64, -13.29) * mm, "end": v(-63.5, -17.78) * mm});
            skPoint(sketch, "E62.visualSharp", {"position": v(-63.5, -64.77) * mm});
            skArc(sketch, "E62.filletArc", {"start": v(-63.5, -58.42) * mm, "mid": v(-61.64, -62.91) * mm, "end": v(-57.15, -64.77) * mm});
            skSolve(sketch);
        }
        {
            var Q0;
            Q0 = qSketchRegion(id + "F25", true);
            extrude(context, id + "F26", {"entities" : qUnion([Q0]), "operationType" : NewBodyOperationType.REMOVE, "oppositeDirection" : true, "depth" : 4.32 * mm, "hasSecondDirection" : true, "secondDirectionOppositeDirection" : false, "secondDirectionDepth" : 5.08 * mm});
        }
        {
            var Q0;
            Q0=makeQuery(id+"F26.boolean.opBoolean","COPY",FACE,{"derivedFrom":makeQuery(id+"F26.opExtrude","SWEPT_FACE",FACE,{"disambiguationData":[OSD([sQuery(id+"F25.wireOp",EDGE,"E58")])]})});
            var sketch = newSketch(context, id + "F27", { "sketchPlane" : qUnion([Q0])});
            skCircle(sketch, "E63", {"center": v(44.45, -3.8) * mm, "radius": 1.52 * mm});
            skSolve(sketch);
        }
        {
            var Q0;
            Q0 = qSketchRegion(id + "F27", true);
            extrude(context, id + "F28", {"entities" : qUnion([Q0]), "operationType" : NewBodyOperationType.REMOVE, "oppositeDirection" : true, "depth" : 25.4 * mm});
        }
        {
            var Q0;
            Q0=makeQuery(id+"F26.boolean.opBoolean","COPY",FACE,{"derivedFrom":makeQuery(id+"F26.opExtrude","SWEPT_FACE",FACE,{"disambiguationData":[OSD([sQuery(id+"F25.wireOp",EDGE,"E58")])]})});
            var sketch = newSketch(context, id + "F29", { "sketchPlane" : qUnion([Q0])});
            skEllipse(sketch, "E64", {"center": v(44.45, -3.8) * mm, "majorRadius": 2.82 * mm, "minorRadius": 1.78 * mm, "majorAxis": v(-1, 0)});
            skSolve(sketch);
        }
        {
            var Q0;
            Q0 = qSketchRegion(id + "F29", true);
            extrude(context, id + "F30", {"entities" : qUnion([Q0]), "operationType" : NewBodyOperationType.REMOVE, "oppositeDirection" : true, "depth" : 2.54 * mm});
        }
        {
            var Q0;
            {var subQ0=makeQuery(id+"F15.boolean.opBoolean","COPY",FACE,{"derivedFrom":makeQuery(id+"F15.opExtrude","SWEPT_FACE",FACE,{"disambiguationData":[OSD([sQuery(id+"F14.wireOp",EDGE,"E22")])]})});Q0=makeQuery(id+"F18.boolean.opBoolean","MERGE",FACE,{"derivedFrom":[subQ0,makeQuery(id+"F18.opPattern","COPY",FACE,{"derivedFrom":subQ0,"instanceName":"1"})]});}
            var sketch = newSketch(context, id + "F31", { "sketchPlane" : qUnion([Q0])});
            skLineSegment(sketch, "E65.bottom", {"start": v(31.75, -23.02) * mm, "end": v(-67.31, -23.02) * mm});
            skLineSegment(sketch, "E65.top", {"start": v(31.75, 40.48) * mm, "end": v(-67.31, 40.48) * mm});
            skLineSegment(sketch, "E65.left", {"start": v(31.75, -23.02) * mm, "end": v(31.75, 40.48) * mm});
            skLineSegment(sketch, "E65.right", {"start": v(-67.31, -23.02) * mm, "end": v(-67.31, 40.48) * mm});
            skSolve(sketch);
        }
        {
            var Q0;
            Q0 = qSketchRegion(id + "F31", true);
            extrude(context, id + "F32", {"entities" : qUnion([Q0]), "depth" : 25.4 * mm});
        }
        {
            var Q0;
            Q0=makeQuery(id+"F32.opExtrude","SWEPT_EDGE",EDGE,{"disambiguationData":[OSD([sQuery(id+"F31.wireOp",EDGE,"E65.top"),sQuery(id+"F31.wireOp",EDGE,"E65.left")])]});
            var Q1;
            Q1=makeQuery(id+"F32.opExtrude","SWEPT_EDGE",EDGE,{"disambiguationData":[OSD([sQuery(id+"F31.wireOp",EDGE,"E65.top"),sQuery(id+"F31.wireOp",EDGE,"E65.right")])]});
            var Q2;
            Q2=makeQuery(id+"F32.opExtrude","SWEPT_EDGE",EDGE,{"disambiguationData":[OSD([sQuery(id+"F31.wireOp",EDGE,"E65.bottom"),sQuery(id+"F31.wireOp",EDGE,"E65.right")])]});
            var Q3;
            Q3=makeQuery(id+"F32.opExtrude","SWEPT_EDGE",EDGE,{"disambiguationData":[OSD([sQuery(id+"F31.wireOp",EDGE,"E65.bottom"),sQuery(id+"F31.wireOp",EDGE,"E65.left")])]});
            fillet(context, id + "F33", {"entities" : qUnion([Q0, Q1, Q2, Q3]), "radius" : 5.08 * mm, "tangentPropagation" : true, "allowEdgeOverflow" : false});
        }
        {
            var Q0;
            Q0=makeQuery(id+"F32.opExtrude","CAP_EDGE",EDGE,{"disambiguationData":[OSD([sQuery(id+"F31.wireOp",EDGE,"E65.top")])],"isStart":false});
            var Q1;
            Q1=makeQuery(id+"F32.opExtrude","CAP_EDGE",EDGE,{"disambiguationData":[OSD([sQuery(id+"F31.wireOp",EDGE,"E65.top")])],"isStart":true});
            fillet(context, id + "F34", {"entities" : qUnion([Q0, Q1]), "radius" : 7.62 * mm, "tangentPropagation" : true, "allowEdgeOverflow" : false});
        }
        {
            var Q0;
            {var subQ0=makeQuery(id+"F15.boolean.opBoolean","COPY",FACE,{"derivedFrom":makeQuery(id+"F15.opExtrude","SWEPT_FACE",FACE,{"disambiguationData":[OSD([sQuery(id+"F14.wireOp",EDGE,"E22")])]})});Q0=makeQuery(id+"F18.boolean.opBoolean","MERGE",FACE,{"derivedFrom":[subQ0,makeQuery(id+"F18.opPattern","COPY",FACE,{"derivedFrom":subQ0,"instanceName":"1"})]});}
            var sketch = newSketch(context, id + "F35", { "sketchPlane" : qUnion([Q0])});
            skLineSegment(sketch, "E66.bottom", {"start": v(31.75, -6.5) * mm, "end": v(-67.31, -6.5) * mm});
            skLineSegment(sketch, "E66.top", {"start": v(31.75, 18.9) * mm, "end": v(-67.31, 18.9) * mm});
            skLineSegment(sketch, "E66.left", {"start": v(31.75, -6.5) * mm, "end": v(31.75, 18.9) * mm});
            skLineSegment(sketch, "E66.right", {"start": v(-67.31, -6.5) * mm, "end": v(-67.31, 18.9) * mm});
            skSolve(sketch);
        }
        {
            var Q0;
            Q0 = qSketchRegion(id + "F35", true);
            extrude(context, id + "F36", {"entities" : qUnion([Q0]), "depth" : 63.5 * mm});
        }
        {
            var Q0;
            Q0=makeQuery(id+"F36.opExtrude","CAP_EDGE",EDGE,{"disambiguationData":[OSD([sQuery(id+"F35.wireOp",EDGE,"E66.left")])],"isStart":false});
            var Q1;
            Q1=makeQuery(id+"F36.opExtrude","CAP_EDGE",EDGE,{"disambiguationData":[OSD([sQuery(id+"F35.wireOp",EDGE,"E66.left")])],"isStart":true});
            var Q2;
            Q2=makeQuery(id+"F36.opExtrude","CAP_EDGE",EDGE,{"disambiguationData":[OSD([sQuery(id+"F35.wireOp",EDGE,"E66.right")])],"isStart":false});
            var Q3;
            Q3=makeQuery(id+"F36.opExtrude","CAP_EDGE",EDGE,{"disambiguationData":[OSD([sQuery(id+"F35.wireOp",EDGE,"E66.right")])],"isStart":true});
            fillet(context, id + "F37", {"entities" : qUnion([Q0, Q1, Q2, Q3]), "radius" : 5.08 * mm, "tangentPropagation" : true, "allowEdgeOverflow" : false});
        }
        {
            var Q0;
            Q0=makeQuery(id+"F36.opExtrude","CAP_EDGE",EDGE,{"disambiguationData":[OSD([sQuery(id+"F35.wireOp",EDGE,"E66.top")])],"isStart":false});
            var Q1;
            Q1=makeQuery(id+"F36.opExtrude","CAP_EDGE",EDGE,{"disambiguationData":[OSD([sQuery(id+"F35.wireOp",EDGE,"E66.bottom")])],"isStart":false});
            fillet(context, id + "F38", {"entities" : qUnion([Q0, Q1]), "radius" : 10.16 * mm, "tangentPropagation" : true, "allowEdgeOverflow" : false});
        }
    });
